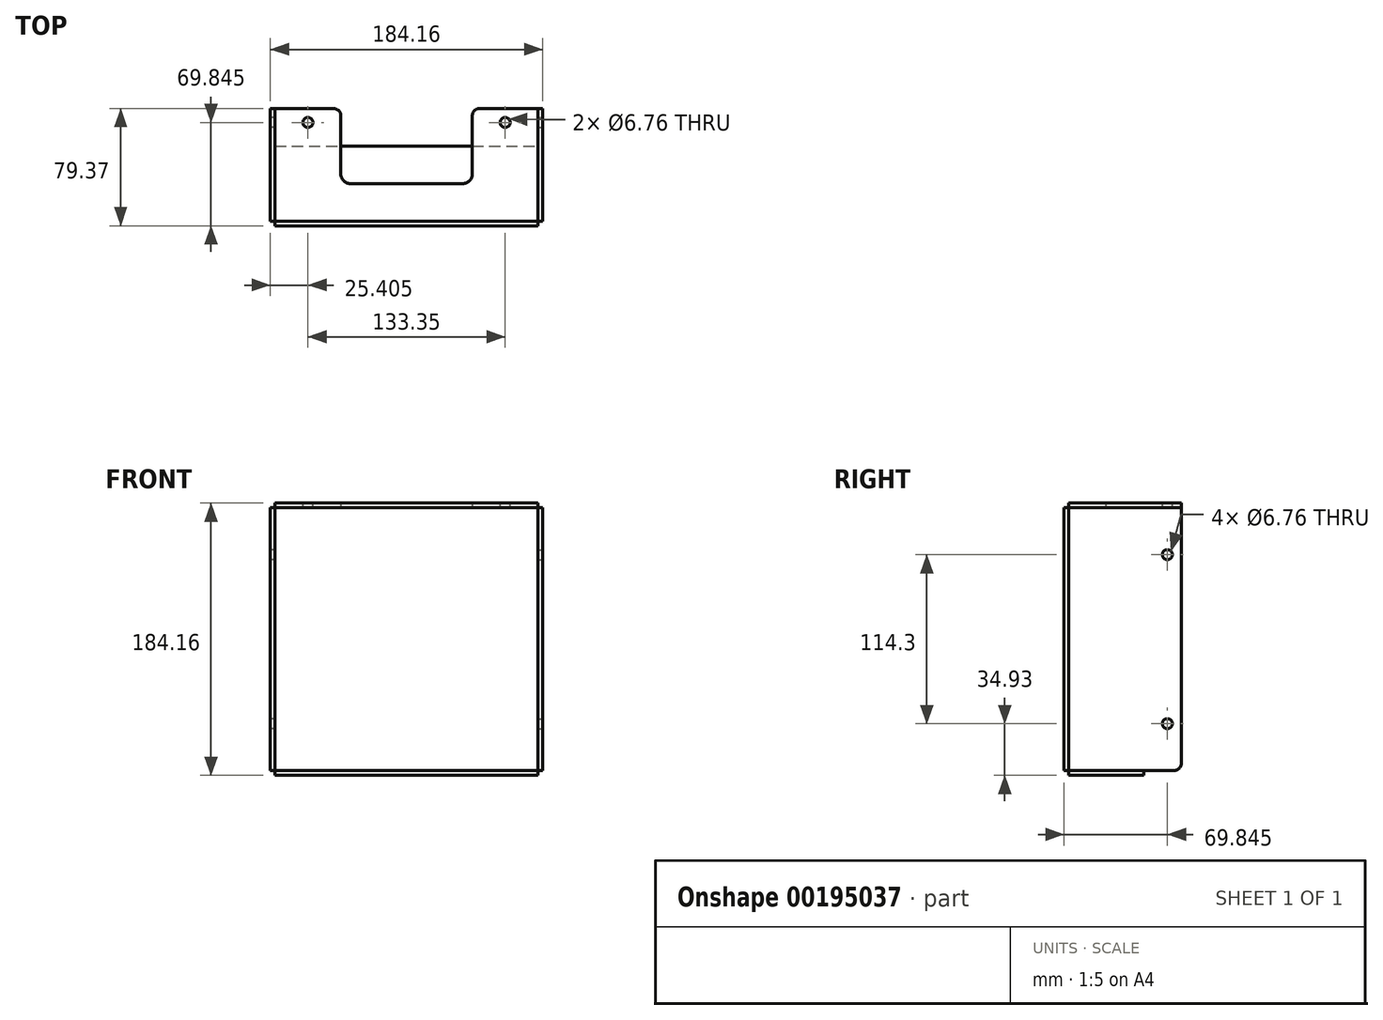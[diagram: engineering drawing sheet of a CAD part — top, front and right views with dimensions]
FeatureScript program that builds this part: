
annotation { "Feature Type Name" : "Feature", "Feature Type Description" : "" }
export const myFeature = defineFeature(function(context is Context, id is Id, definition is map)
    precondition{}
    {
        {
            var Q0;
            Q0=qCreatedBy(makeId("Front.planeOp"),FACE);
            var sketch = newSketch(context, id + "F0", { "sketchPlane" : qUnion([Q0])});
            skLineSegment(sketch, "E0.bottom", {"start": v(-88.9, 88.9) * mm, "end": v(88.9, 88.9) * mm});
            skLineSegment(sketch, "E0.top", {"start": v(-88.9, -88.9) * mm, "end": v(88.9, -88.9) * mm});
            skLineSegment(sketch, "E0.left", {"start": v(-88.9, 88.9) * mm, "end": v(-88.9, -88.9) * mm});
            skLineSegment(sketch, "E0.right", {"start": v(88.9, 88.9) * mm, "end": v(88.9, -88.9) * mm});
            skPoint(sketch, "E0.middle", {"position": v(0, 0) * mm});
            skSolve(sketch);
        }
        {
            var Q0;
            Q0 = qSketchRegion(id + "F0", true);
            extrude(context, id + "F1", {"entities" : qUnion([Q0]), "depth" : 3.17 * mm});
        }
        {
            var Q0;
            Q0=makeQuery(id+"F1.opExtrude","CAP_FACE",FACE,{"disambiguationData":[OSD([sQuery(id+"F0.wireOp",EDGE,"E0.bottom"),sQuery(id+"F0.wireOp",EDGE,"E0.top"),sQuery(id+"F0.wireOp",EDGE,"E0.left"),sQuery(id+"F0.wireOp",EDGE,"E0.right")])],"isStart":true});
            var sketch = newSketch(context, id + "F2", { "sketchPlane" : qUnion([Q0])});
            skLineSegment(sketch, "E1.bottom", {"start": v(-88.9, 88.9) * mm, "end": v(88.9, 88.9) * mm});
            skLineSegment(sketch, "E1.top", {"start": v(-88.9, 92.08) * mm, "end": v(88.9, 92.08) * mm});
            skLineSegment(sketch, "E1.left", {"start": v(-88.9, 88.9) * mm, "end": v(-88.9, 92.08) * mm});
            skLineSegment(sketch, "E1.right", {"start": v(88.9, 88.9) * mm, "end": v(88.9, 92.08) * mm});
            skLineSegment(sketch, "E2.bottom", {"start": v(-88.9, 88.9) * mm, "end": v(-92.08, 88.9) * mm});
            skLineSegment(sketch, "E2.top", {"start": v(-88.9, -88.9) * mm, "end": v(-92.07, -88.9) * mm});
            skLineSegment(sketch, "E2.left", {"start": v(-88.9, 88.9) * mm, "end": v(-88.9, -88.9) * mm});
            skLineSegment(sketch, "E2.right", {"start": v(-92.08, 88.9) * mm, "end": v(-92.07, -88.9) * mm});
            skLineSegment(sketch, "E3.bottom", {"start": v(88.9, 88.9) * mm, "end": v(92.07, 88.9) * mm});
            skLineSegment(sketch, "E3.top", {"start": v(88.9, -88.9) * mm, "end": v(92.07, -88.9) * mm});
            skLineSegment(sketch, "E3.left", {"start": v(88.9, 88.9) * mm, "end": v(88.9, -88.9) * mm});
            skLineSegment(sketch, "E3.right", {"start": v(92.07, 88.9) * mm, "end": v(92.07, -88.9) * mm});
            skSolve(sketch);
        }
        {
            var Q0;
            Q0 = qSketchRegion(id + "F2", true);
            extrude(context, id + "F3", {"entities" : qUnion([Q0]), "depth" : 76.2 * mm});
        }
        {
            var Q0;
            Q0=makeQuery(id+"F1.opExtrude","CAP_FACE",FACE,{"disambiguationData":[OSD([sQuery(id+"F0.wireOp",EDGE,"E0.bottom"),sQuery(id+"F0.wireOp",EDGE,"E0.top"),sQuery(id+"F0.wireOp",EDGE,"E0.left"),sQuery(id+"F0.wireOp",EDGE,"E0.right")])],"isStart":true});
            var sketch = newSketch(context, id + "F4", { "sketchPlane" : qUnion([Q0])});
            skLineSegment(sketch, "E4.bottom", {"start": v(-88.9, -88.9) * mm, "end": v(88.9, -88.9) * mm});
            skLineSegment(sketch, "E4.top", {"start": v(-88.9, -92.07) * mm, "end": v(88.9, -92.07) * mm});
            skLineSegment(sketch, "E4.left", {"start": v(-88.9, -88.9) * mm, "end": v(-88.9, -92.07) * mm});
            skLineSegment(sketch, "E4.right", {"start": v(88.9, -88.9) * mm, "end": v(88.9, -92.07) * mm});
            skSolve(sketch);
        }
        {
            var Q0;
            Q0 = qSketchRegion(id + "F4", true);
            extrude(context, id + "F5", {"entities" : qUnion([Q0]), "depth" : 50.8 * mm});
        }
        {
            var Q0;
            Q0=makeQuery(id+"F3.opExtrude","SWEPT_FACE",FACE,{"disambiguationData":[OSD([sQuery(id+"F2.wireOp",EDGE,"E1.top")])]});
            var sketch = newSketch(context, id + "F6", { "sketchPlane" : qUnion([Q0])});
            skLineSegment(sketch, "E5.bottom", {"start": v(44.45, 25.4) * mm, "end": v(-44.45, 25.4) * mm});
            skLineSegment(sketch, "E5.top", {"start": v(44.45, 127) * mm, "end": v(-44.45, 127) * mm});
            skLineSegment(sketch, "E5.left", {"start": v(44.45, 25.4) * mm, "end": v(44.45, 127) * mm});
            skLineSegment(sketch, "E5.right", {"start": v(-44.45, 25.4) * mm, "end": v(-44.45, 127) * mm});
            skPoint(sketch, "E5.middle", {"position": v(0, 76.2) * mm});
            skSolve(sketch);
        }
        {
            var Q0;
            Q0 = qSketchRegion(id + "F6", true);
            extrude(context, id + "F7", {"entities" : qUnion([Q0]), "operationType" : NewBodyOperationType.REMOVE, "oppositeDirection" : true, "depth" : 25.4 * mm});
        }
        {
            var Q0;
            Q0=makeQuery(id+"F7.boolean.opBoolean","COPY",EDGE,{"derivedFrom":makeQuery(id+"F7.opExtrude","SWEPT_EDGE",EDGE,{"disambiguationData":[OSD([sQuery(id+"F6.wireOp",EDGE,"E5.bottom"),sQuery(id+"F6.wireOp",EDGE,"E5.right")])]})});
            var Q1;
            Q1=makeQuery(id+"F7.boolean.opBoolean","COPY",EDGE,{"derivedFrom":makeQuery(id+"F7.opExtrude","SWEPT_EDGE",EDGE,{"disambiguationData":[OSD([sQuery(id+"F6.wireOp",EDGE,"E5.bottom"),sQuery(id+"F6.wireOp",EDGE,"E5.left")])]})});
            fillet(context, id + "F8", {"entities" : qUnion([Q0, Q1]), "radius" : 6.35 * mm, "tangentPropagation" : true, "allowEdgeOverflow" : false});
        }
        {
            var Q0;
            Q0=makeQuery(id+"F7.boolean.opBoolean","INTERSECT",EDGE,{"derivedFrom":[makeQuery(id+"F3.opExtrude","CAP_FACE",FACE,{"disambiguationData":[OSD([sQuery(id+"F2.wireOp",EDGE,"E1.bottom"),sQuery(id+"F2.wireOp",EDGE,"E1.top"),sQuery(id+"F2.wireOp",EDGE,"E1.left"),sQuery(id+"F2.wireOp",EDGE,"E1.right")])],"isStart":false}),makeQuery(id+"F7.opExtrude","SWEPT_FACE",FACE,{"disambiguationData":[OSD([sQuery(id+"F6.wireOp",EDGE,"E5.right")])]})]});
            var Q1;
            Q1=makeQuery(id+"F7.boolean.opBoolean","INTERSECT",EDGE,{"derivedFrom":[makeQuery(id+"F3.opExtrude","CAP_FACE",FACE,{"disambiguationData":[OSD([sQuery(id+"F2.wireOp",EDGE,"E1.bottom"),sQuery(id+"F2.wireOp",EDGE,"E1.top"),sQuery(id+"F2.wireOp",EDGE,"E1.left"),sQuery(id+"F2.wireOp",EDGE,"E1.right")])],"isStart":false}),makeQuery(id+"F7.opExtrude","SWEPT_FACE",FACE,{"disambiguationData":[OSD([sQuery(id+"F6.wireOp",EDGE,"E5.left")])]})]});
            fillet(context, id + "F9", {"entities" : qUnion([Q0, Q1]), "radius" : 5.08 * mm, "tangentPropagation" : true, "allowEdgeOverflow" : false});
        }
        {
            var Q0;
            Q0=makeQuery(id+"F3.opExtrude","CAP_EDGE",EDGE,{"disambiguationData":[OSD([sQuery(id+"F2.wireOp",EDGE,"E2.top")])],"isStart":false});
            var Q1;
            Q1=makeQuery(id+"F3.opExtrude","CAP_EDGE",EDGE,{"disambiguationData":[OSD([sQuery(id+"F2.wireOp",EDGE,"E3.top")])],"isStart":false});
            fillet(context, id + "F10", {"entities" : qUnion([Q0, Q1]), "radius" : 5.08 * mm, "tangentPropagation" : true, "allowEdgeOverflow" : false});
        }
        {
            var Q0;
            Q0=makeQuery(id+"F3.opExtrude","SWEPT_FACE",FACE,{"disambiguationData":[OSD([sQuery(id+"F2.wireOp",EDGE,"E1.top")])]});
            var sketch = newSketch(context, id + "F11", { "sketchPlane" : qUnion([Q0])});
            skLineSegment(sketch, "E6", {"start": v(0, -105.7) * mm, "end": v(0, 127.8) * mm, "construction": true});
            skLineSegment(sketch, "E7", {"start": v(-88.9, 76.2) * mm, "end": v(117.43, 76.2) * mm, "construction": true});
            skLineSegment(sketch, "E8.0", {"start": v(-66.68, -105.7) * mm, "end": v(-66.68, 127.8) * mm, "construction": true});
            skLineSegment(sketch, "E9.0", {"start": v(-88.9, 66.67) * mm, "end": v(117.43, 66.68) * mm, "construction": true});
            skPoint(sketch, "E10", {"position": v(-66.68, 66.67) * mm});
            skPoint(sketch, "E11.MirrorP", {"position": v(66.68, 66.67) * mm});
            skSolve(sketch);
        }
        {
            var Q0;
            Q0=sQuery(id+"F11.wireOp",VERTEX,"E10");
            var Q1;
            Q1=sQuery(id+"F11.wireOp",VERTEX,"E11.MirrorP");
            var Q2;
            Q2=makeQuery(id+"F3.opExtrude","SWEPT_BODY",BODY,{"disambiguationData":[OSD([sQuery(id+"F2.wireOp",EDGE,"E1.bottom"),sQuery(id+"F2.wireOp",EDGE,"E1.top"),sQuery(id+"F2.wireOp",EDGE,"E1.left"),sQuery(id+"F2.wireOp",EDGE,"E1.right")])]});
            hole(context, id + "F12", {"style" : HoleStyle.SIMPLE, "endStyle" : HoleEndStyle.BLIND, "standardTappedOrClearance" : lookupTablePath({ "standard" : "ANSI", "fit" : "Normal (ASME)", "size" : "1/4", "type" : "Clearance" }), "standardBlindInLast" : lookupTablePath({ "fit" : "Free", "standard" : "ANSI", "size" : "1/4", "type" : "Clearance" }), "holeDiameter" : 6.76 * mm, "holeDepth" : 19.05 * mm, "locations" : qUnion([Q0, Q1]), "scope" : qUnion([Q2])});
        }
        {
            var Q0;
            Q0=makeQuery(id+"F3.opExtrude","SWEPT_FACE",FACE,{"disambiguationData":[OSD([sQuery(id+"F2.wireOp",EDGE,"E2.right")])]});
            var sketch = newSketch(context, id + "F13", { "sketchPlane" : qUnion([Q0])});
            skLineSegment(sketch, "E12.0", {"start": v(76.2, 88.9) * mm, "end": v(76.2, -83.82) * mm, "construction": true});
            skLineSegment(sketch, "E13.0", {"start": v(66.68, 88.9) * mm, "end": v(66.68, -83.82) * mm, "construction": true});
            skLineSegment(sketch, "E14.0", {"start": v(76.2, 88.9) * mm, "end": v(0, 88.9) * mm, "construction": true});
            skLineSegment(sketch, "E15.0", {"start": v(76.2, 57.15) * mm, "end": v(0, 57.15) * mm, "construction": true});
            skLineSegment(sketch, "E16.0", {"start": v(76.2, -57.15) * mm, "end": v(0, -57.15) * mm, "construction": true});
            skPoint(sketch, "E17", {"position": v(66.68, 57.15) * mm});
            skPoint(sketch, "E18", {"position": v(66.68, -57.15) * mm});
            skSolve(sketch);
        }
        {
            var Q0;
            Q0=sQuery(id+"F13.wireOp",VERTEX,"E17");
            var Q1;
            Q1=sQuery(id+"F13.wireOp",VERTEX,"E18");
            var Q2;
            Q2=makeQuery(id+"F3.opExtrude","SWEPT_BODY",BODY,{"disambiguationData":[OSD([sQuery(id+"F2.wireOp",EDGE,"E2.bottom"),sQuery(id+"F2.wireOp",EDGE,"E2.top"),sQuery(id+"F2.wireOp",EDGE,"E2.left"),sQuery(id+"F2.wireOp",EDGE,"E2.right")])]});
            hole(context, id + "F14", {"style" : HoleStyle.SIMPLE, "endStyle" : HoleEndStyle.BLIND, "standardTappedOrClearance" : lookupTablePath({ "standard" : "ANSI", "fit" : "Normal (ASME)", "size" : "1/4", "type" : "Clearance" }), "standardBlindInLast" : lookupTablePath({ "fit" : "Free", "standard" : "ANSI", "size" : "1/4", "type" : "Clearance" }), "holeDiameter" : 6.76 * mm, "holeDepth" : 19.05 * mm, "locations" : qUnion([Q0, Q1]), "scope" : qUnion([Q2])});
        }
        {
            var Q0;
            Q0=makeQuery(id+"F3.opExtrude","SWEPT_FACE",FACE,{"disambiguationData":[OSD([sQuery(id+"F2.wireOp",EDGE,"E3.right")])]});
            var sketch = newSketch(context, id + "F15", { "sketchPlane" : qUnion([Q0])});
            skCircle(sketch, "E19.0", {"center": v(-66.68, 57.15) * mm, "radius": 3.38 * mm, "construction": true});
            skCircle(sketch, "E20.0", {"center": v(-66.68, -57.15) * mm, "radius": 3.38 * mm, "construction": true});
            skSolve(sketch);
        }
        {
            var Q0;
            Q0=sQuery(id+"F15.wireOp",VERTEX,"E19.0.center");
            var Q1;
            Q1=sQuery(id+"F15.wireOp",VERTEX,"E20.0.center");
            var Q2;
            Q2=makeQuery(id+"F3.opExtrude","SWEPT_BODY",BODY,{"disambiguationData":[OSD([sQuery(id+"F2.wireOp",EDGE,"E3.bottom"),sQuery(id+"F2.wireOp",EDGE,"E3.top"),sQuery(id+"F2.wireOp",EDGE,"E3.left"),sQuery(id+"F2.wireOp",EDGE,"E3.right")])]});
            hole(context, id + "F16", {"style" : HoleStyle.SIMPLE, "endStyle" : HoleEndStyle.BLIND, "standardTappedOrClearance" : lookupTablePath({ "standard" : "ANSI", "fit" : "Normal (ASME)", "size" : "1/4", "type" : "Clearance" }), "standardBlindInLast" : lookupTablePath({ "fit" : "Free", "standard" : "ANSI", "size" : "1/4", "type" : "Clearance" }), "holeDiameter" : 6.76 * mm, "holeDepth" : 19.05 * mm, "locations" : qUnion([Q0, Q1]), "scope" : qUnion([Q2])});
        }
    });
